# Revit family: Hager-Vega_D-IP40-syst-BE-fr
name_source: partatom
category: Electrical Equipment
units: mm (PartAtom-declared; Revit-internal decimal feet)

## family parameters
Cut with Voids When Loaded = No
Host = Face
Panel Configuration = Two Columns, Circuits Across
Part Type = Panelboard
Room Calculation Point = No
Round Connector Dimension = Use Diameter
Shared = No

## types (12) — shared parameters
EF000003 - mode de pose = EV000383 - encastré
EF000007 - couleur = EV000202 - blanc
EF000008 - largeur = 600 mm
EF000049 - profondeur = 150 mm  [stored 0.492126 ft]
EF000116 - numéro RAL = 9010
EF000118 - avec cadre/support de montage = No
EF000218 - profondeur d'encastrement = 150 mm  [stored 0.492126 ft]
EF000339 - type de capot = EV004216 - porte
EF000846 - largeur d'encastrement = 550 mm
EF001062 - finition CEM = No
EF001088 - possibilité de montage en saillie = Yes
EF001131 - profondeur intérieure = 110 mm
EF001134 - rail DIN = Yes
EF001596 - matériau du boîtier/corps = EV000154 - autre
EF002950 - largeur en nombre de modules = 24
EF005474 - indice de protection (IP) = EV006415 - IP40
EF006306 - avec serrure = No
EF015776 - borne de mise à la terre = No
EF015777 - borne à conducteur neutre = No
EF015941 - porte pour transmission du signal = No
HG000001 - nombre de colonnes = 1
HG000002 - avec porte = Yes
HG000003 - Gamme = Vega D
HG000005 - Epaisseur = 3 mm  [stored 0.00984252 ft]
HG000006 - Encastré = Yes
HG000009 - Porte à double battant = No
HG000010 - Portes asymétriques = No
HG000011 - Rangées du bas vides = No
HG000017 - Distance entre pôles = 18 mm  [stored 0.0590551 ft]
Manufacturer = Hager
Type Comments = Vega D
zero-valued in all types: Default Elevation, HG000007 - Nombre de colonnes vides, HG000008 - Nombre de rangées vides

## per-type parameters (varying)
| type | EF000040 - hauteur | EF000266 - nombre de rangées | EF000332 - hauteur d'encastrement | EF006244 - couvercle/porte transparent(e) | EF009212 - finition du couvercle | HG000004 - Référence fabricant | Model |
| Encastré IP40 L600 H1137 P150 24 Modules - FU62BN | 1137 mm | 6 | 1137 mm | No | EV000116 - fermé | FU62BN | FU62BN |
| Encastré IP40 L600 H1137 P150 24 Modules - FU62CN | 1137 mm | 6 | 1137 mm | Yes | EV009916 - avec échancrure | FU62CN | FU62CN |
| Encastré IP40 L600 H1287 P150 24 Modules - FU72BN | 1287 mm | 7 | 1287 mm | No | EV000116 - fermé | FU72BN | FU72BN |
| Encastré IP40 L600 H1287 P150 24 Modules - FU72CN | 1287 mm | 7 | 1287 mm | Yes | EV009916 - avec échancrure | FU72CN | FU72CN |
| Encastré IP40 L600 H537 P150 24 Modules - FU22BN | 537 mm | 2 | 537 mm | No | EV000116 - fermé | FU22BN | FU22BN |
| Encastré IP40 L600 H537 P150 24 Modules - FU22CN | 537 mm | 2 | 537 mm | Yes | EV009916 - avec échancrure | FU22CN | FU22CN |
| Encastré IP40 L600 H687 P150 24 Modules - FU32BN | 687 mm | 3 | 687 mm | No | EV000116 - fermé | FU32BN | FU32BN |
| Encastré IP40 L600 H687 P150 24 Modules - FU32CN | 687 mm | 3 | 687 mm | Yes | EV009916 - avec échancrure | FU32CN | FU32CN |
| Encastré IP40 L600 H837 P150 24 Modules - FU42BN | 837 mm | 4 | 837 mm | No | EV000116 - fermé | FU42BN | FU42BN |
| Encastré IP40 L600 H837 P150 24 Modules - FU42CN | 837 mm | 4 | 837 mm | Yes | EV009916 - avec échancrure | FU42CN | FU42CN |
| Encastré IP40 L600 H987 P150 24 Modules - FU52BN | 987 mm  [stored 3.23819 ft] | 5 | 987 mm  [stored 3.23819 ft] | No | EV000116 - fermé | FU52BN | FU52BN |
| Encastré IP40 L600 H987 P150 24 Modules - FU52CN | 987 mm  [stored 3.23819 ft] | 5 | 987 mm  [stored 3.23819 ft] | Yes | EV009916 - avec échancrure | FU52CN | FU52CN |

note: [stored X ft] marks values corroborated as IEEE doubles in the binary element streams (Revit-internal decimal feet)

## geometry (parser evidence)
native form markers: Sweep x17
no freeform markers — native parametric forms only
